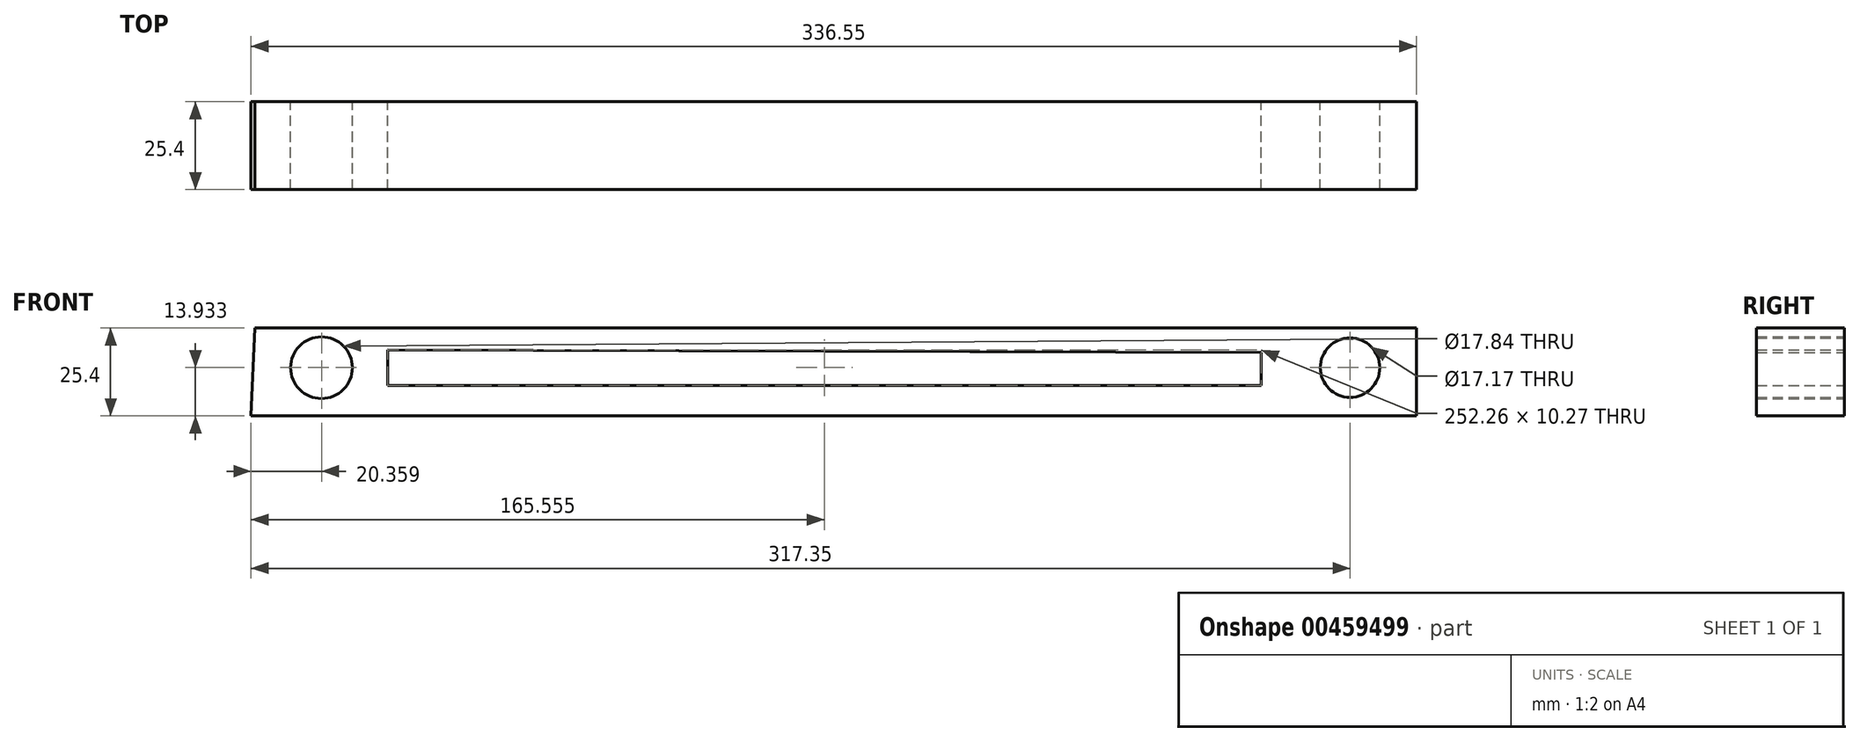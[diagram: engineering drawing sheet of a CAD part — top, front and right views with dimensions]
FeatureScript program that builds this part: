
annotation { "Feature Type Name" : "Feature", "Feature Type Description" : "" }
export const myFeature = defineFeature(function(context is Context, id is Id, definition is map)
    precondition{}
    {
        {
            var Q0;
            Q0=qCreatedBy(makeId("Front.planeOp"),FACE);
            var sketch = newSketch(context, id + "F0", { "sketchPlane" : qUnion([Q0])});
            skLineSegment(sketch, "E0", {"start": v(-105.83, 25.4) * mm, "end": v(229.66, 25.4) * mm});
            skLineSegment(sketch, "E1", {"start": v(229.66, 25.4) * mm, "end": v(229.66, 0) * mm});
            skLineSegment(sketch, "E2", {"start": v(229.66, 0) * mm, "end": v(-106.9, 0) * mm});
            skLineSegment(sketch, "E3", {"start": v(-106.9, 0) * mm, "end": v(-105.83, 25.4) * mm});
            skCircle(sketch, "E4", {"center": v(-86.53, 13.93) * mm, "radius": 8.92 * mm});
            skCircle(sketch, "E5", {"center": v(210.46, 13.93) * mm, "radius": 8.58 * mm});
            skLineSegment(sketch, "E6", {"start": v(-67.46, 19.07) * mm, "end": v(-67.46, 8.8) * mm});
            skLineSegment(sketch, "E7", {"start": v(-67.46, 8.8) * mm, "end": v(184.8, 8.8) * mm});
            skLineSegment(sketch, "E8", {"start": v(184.8, 8.8) * mm, "end": v(184.8, 18.33) * mm});
            skLineSegment(sketch, "E9", {"start": v(184.8, 18.33) * mm, "end": v(-67.46, 19.07) * mm});
            skPoint(sketch, "E10", {"position": v(-105.83, 25.4) * mm});
            skSolve(sketch);
        }
        {
            var Q0;
            Q0 = qSketchRegion(id + "F0", true);
            extrude(context, id + "F1", {"entities" : qUnion([Q0]), "depth" : 25.4 * mm});
        }
    });
